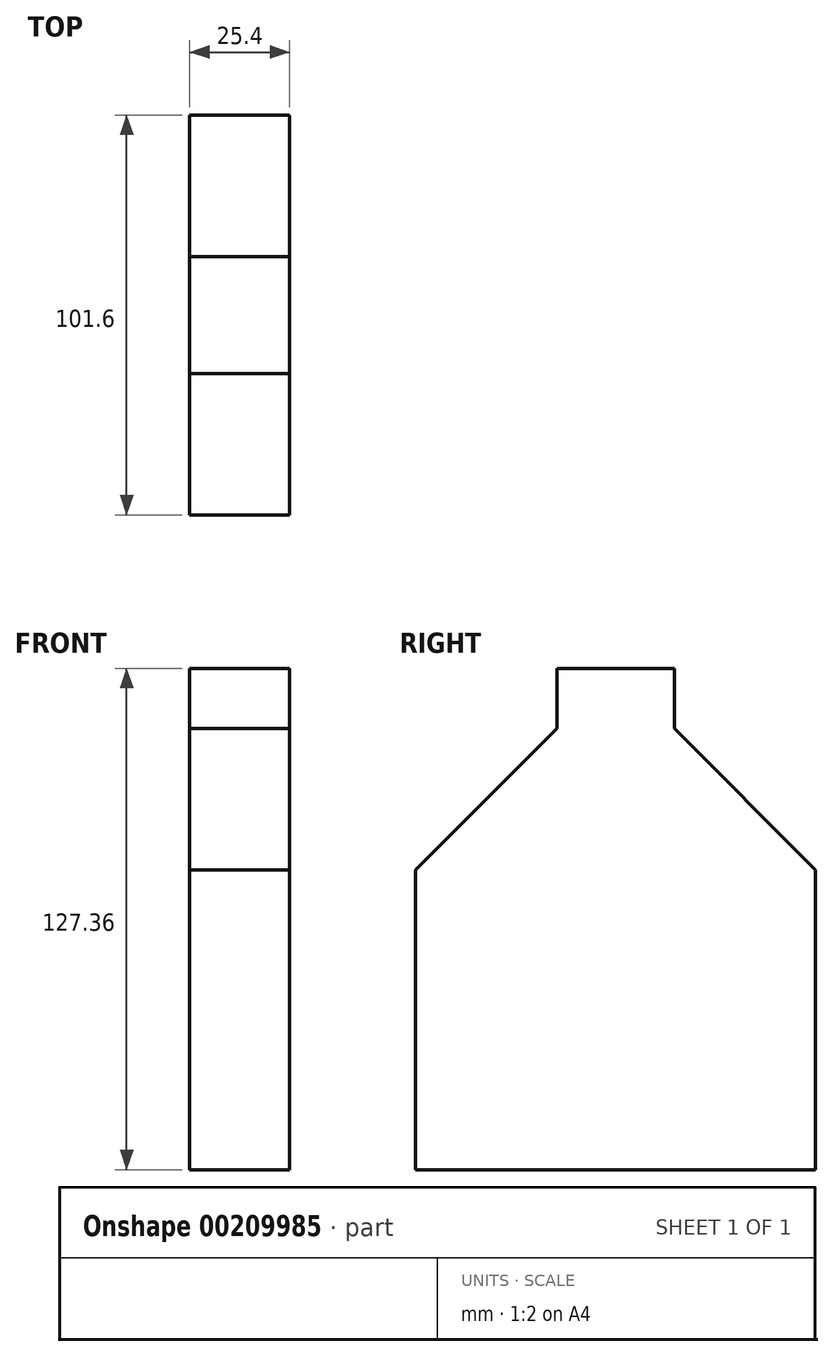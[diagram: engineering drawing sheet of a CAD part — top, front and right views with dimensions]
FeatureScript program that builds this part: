
annotation { "Feature Type Name" : "Feature", "Feature Type Description" : "" }
export const myFeature = defineFeature(function(context is Context, id is Id, definition is map)
    precondition{}
    {
        {
            var Q0;
            Q0=qCreatedBy(makeId("Right.planeOp"),FACE);
            var sketch = newSketch(context, id + "F0", { "sketchPlane" : qUnion([Q0])});
            skLineSegment(sketch, "E0.bottom", {"start": v(-50.8, -67.93) * mm, "end": v(50.8, -67.93) * mm});
            skLineSegment(sketch, "E0.left", {"start": v(-50.8, -67.93) * mm, "end": v(-50.8, 8.27) * mm});
            skLineSegment(sketch, "E0.right", {"start": v(50.8, -67.93) * mm, "end": v(50.8, 8.27) * mm});
            skPoint(sketch, "E0.middle", {"position": v(0, -29.83) * mm});
            skLineSegment(sketch, "E1", {"start": v(50.8, 8.27) * mm, "end": v(14.88, 44.2) * mm});
            skLineSegment(sketch, "E2", {"start": v(14.88, 44.2) * mm, "end": v(14.88, 59.43) * mm});
            skLineSegment(sketch, "E3", {"start": v(14.88, 59.43) * mm, "end": v(0, 59.43) * mm});
            skLineSegment(sketch, "E4.MirrorCS", {"start": v(-14.88, 59.43) * mm, "end": v(0, 59.43) * mm});
            skLineSegment(sketch, "E5.MirrorCS", {"start": v(-14.88, 44.2) * mm, "end": v(-14.88, 59.43) * mm});
            skLineSegment(sketch, "E6.MirrorCS", {"start": v(-50.8, 8.27) * mm, "end": v(-14.88, 44.2) * mm});
            skSolve(sketch);
        }
        {
            var Q0;
            Q0 = qSketchRegion(id + "F0", true);
            extrude(context, id + "F1", {"entities" : qUnion([Q0]), "depth" : 25.4 * mm});
        }
    });
